# Revit family: Grab_Bar-90_Degree-Bobrick-B-5898_Series
name_source: partatom
category: Specialty Equipment
revit_build: Autodesk Revit 2014 (Build: 20130308_1515(x64)
units: mm (PartAtom-declared; Revit-internal decimal feet)

## types (2) — shared parameters
ADA Compliant = Yes
Assembly Code = E2010
Default Elevation = 36"
Diameter = 1 1/4"
Height = 30"
Installation Type = Wall Mounted
Manufacturer = Bobrick Washroom Equipment, Inc.
Material = Stainless Steel-Bobrick-Type 304-Satin
Price = Prices may vary. Please consult Manufacturer Representative for most up-to-date price list.
Product Documentation Link = http://bobrick.com
Product Page URL = http://bobrick.com
Safety Warning = Grab bars are no stronger than the anchors and walls to which they are attached and, therefore, must be firmly secured in order to support the loads for which they are intended. To avoid potential injury, the building owner or maintenance personnel should remove the grab bar from service if the grab bar is not adequately secured to wall or if there is any observed damage to the welds.
URL = http://bobrick.com
Warranty Information = 1 Year Limited Warranty
Width = 30"

## per-type parameters (varying)
| type | Description | Specification |
| B-5898 | 1-1/4" (32mm) Diameter Stainless Steel 30"x 30" (762x762mm) 90 Degree Grab Bar | Grab bar shall be type-304 stainless steel with satin-finish. Grab bar shall have 18-gauge (1.2mm) wall thickness and 1-1/4" (32mm) outside diameter. Clearance between the grab bar and wall shall be 1-1/2" (38mm). Concealed mounting flanges shall be 1/8" (3mm) thick stainless steel plate, 2" x 3-1/8" (50 x 80mm), and equipped with two screw holes for attachment to wall. Flange covers shall be 22-gauge (0.8mm) stainless steel, 3-1/4" (85mm) diameter, and shall snap over mounting flanges to conceal mounting screws and/or WingIt fasteners. Ends of grab bar shall pass through concealed mounting flanges and be heliarc welded to form one structural unit. Grab bar shall comply with accessible design (including ADAAG in the U.S.A.) for structural strength. |
| B-5898.99 | 1-1/4" (32mm) Diameter Stainless Steel 30"x 30" (762x762mm) 90 Degree Grab Bar with Peened Gripping Surface | Grab bar shall be type-304 stainless steel with satin-finish. Grab bar shall have 18-gauge (1.2mm) wall thickness and 1-1/4" (32mm) outside diameter with peened gripping surface. Clearance between the grab bar and wall shall be 1-1/2" (38mm). Concealed mounting flanges shall be 1/8" (3mm) thick stainless steel plate, 2" x 3-1/8" (50 x 80mm), and equipped with two screw holes for attachment to wall. Flange covers shall be 22-gauge (0.8mm) stainless steel, 3-1/4" (85mm) diameter, and shall snap over mounting flanges to conceal mounting screws and/or WingIt fasteners. Ends of grab bar shall pass through concealed mounting flanges and be heliarc welded to form one structural unit. Grab bar shall comply with accessible design (including ADAAG in the U.S.A.) for structural strength. |

note: column(s) folded — value = type name in every type: Model

## geometry (parser evidence)
native form markers: Sweep x2
no freeform markers — native parametric forms only
